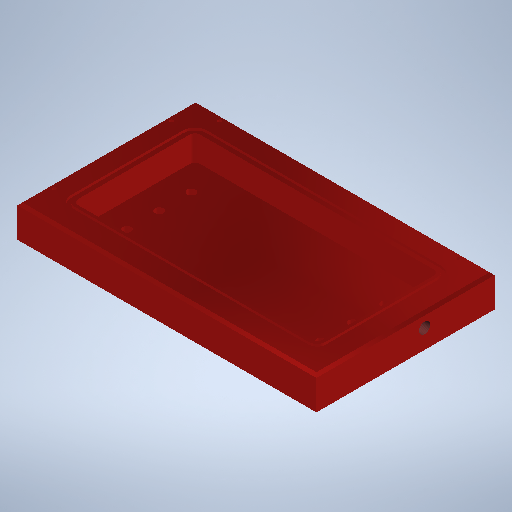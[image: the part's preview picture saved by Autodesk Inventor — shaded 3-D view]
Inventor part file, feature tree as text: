
AUTODESK INVENTOR PART (.ipt)
format: ipt  version: 2025 (Build 290162000, 162)  size: 341,504 bytes
history: native  units: mm
features: extrude x3, sketch x3, hole x3, fillet x1, chamfer x1
ambient origin geometry x8: Origin, YZ Plane, XZ Plane, XY Plane, X Axis, Y Axis, Z Axis, Center Point
bodies: Volumenkörper1 (feature_tree)
feature tree (11):
  extrude  "Extrusion1"  Depth=140.0mm
  extrude  "Extrusion2"  Depth=192.0mm
  fillet  "Rundung1"  Radius=96.0mm
  chamfer  "Fase1"  Distance=20.0mm
  sketch  "Skizze4"  dims[d10=4.0mm d11=2.0mm d12=2.0mm d13=45.0deg d153=24.0mm d154=24.0mm d155=5.0mm d158=5.0mm d159=5.0mm d160=24.0mm d161=24.0mm d162=5.0mm d169=3.0mm d170=6.0mm d171=8.0mm d172=4.6mm d173=14.3117mm d174=20.0mm d175=20.594885mm d193=76.2mm d194=76.2mm d195=6.756mm d196=6.924mm d197=12.878mm d198=2.0mm d199=14.3117mm d200=8.0mm d201=20.594885mm d202=25.4mm d203=25.4mm d204=25.4mm d205=25.4mm d206=55.0mm d207=15.0mm d208=7.95mm d209=6.924mm d210=0.624793mm d211=8.304mm d212=12.878mm d213=2.0mm d214=14.3117mm d215=11.628mm d216=20.594885mm d220=2.5mm d221=2.5mm d222=2.5mm d225=3.0mm d226=3.0mm d227=1.905mm d228=0.0mm]
  hole  "Bohrung7"  [1 undecoded]
  hole  "Hole9"  [1 undecoded]
  hole  "Hole10"  [1 undecoded]
  extrude  "Extrusion5"  Depth=1.905mm
  sketch  "Skizze1"  dims[d0=235.0mm d2=140.0mm]
  sketch  "Skizze2"  dims[d3=25.4mm d4=0.0mm d5=192.0mm d7=96.0mm d8=20.0mm d9=0.0mm]
note: 3 required parameter values undecoded (feature->parameter linkage not recoverable at this tier; creation-order binding heuristic only, values carry confidence <= 0.55)
